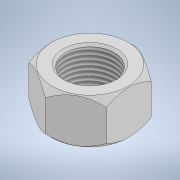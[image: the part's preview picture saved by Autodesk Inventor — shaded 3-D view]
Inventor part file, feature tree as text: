
AUTODESK INVENTOR PART (.ipt)
format: ipt  version: 2020 (Build 240168000, 168)  size: 141,312 bytes
history: native  units: mm
features: sketch x3, extrude x1, revolve x1, plane x1, mirror x1, hole x1, chamfer x1
ambient origin geometry x8: Origin, YZ Plane, XZ Plane, XY Plane, X Axis, Y Axis, Z Axis, Center Point
bodies: Solid1 (feature_tree)
feature tree (9):
  extrude  "Extrusion1"  Depth=10.0mm TaperAngle=0.0deg
  revolve  "Revolution1"  Angle=45.0deg
  plane  "Work Plane1"
  mirror  "Mirror1"
  hole  "Hole1"  [1 undecoded]
  chamfer  "Chamfer1"  [1 undecoded]
  sketch  "Sketch1"  dims[d1=20.0mm d2=10.0mm d3=0.0mm]
  sketch  "Sketch2"  dims[d6=90.0deg]
  sketch  "Sketch3"  dims[d7=10.917mm d8=24.0mm d9=4.0mm d10=2.0mm d11=90.0deg d12=29.1mm d13=20.594885mm d14=0.5mm d15=2.0mm d16=45.0deg]
note: 2 required parameter values undecoded (feature->parameter linkage not recoverable at this tier; creation-order binding heuristic only, values carry confidence <= 0.55)
